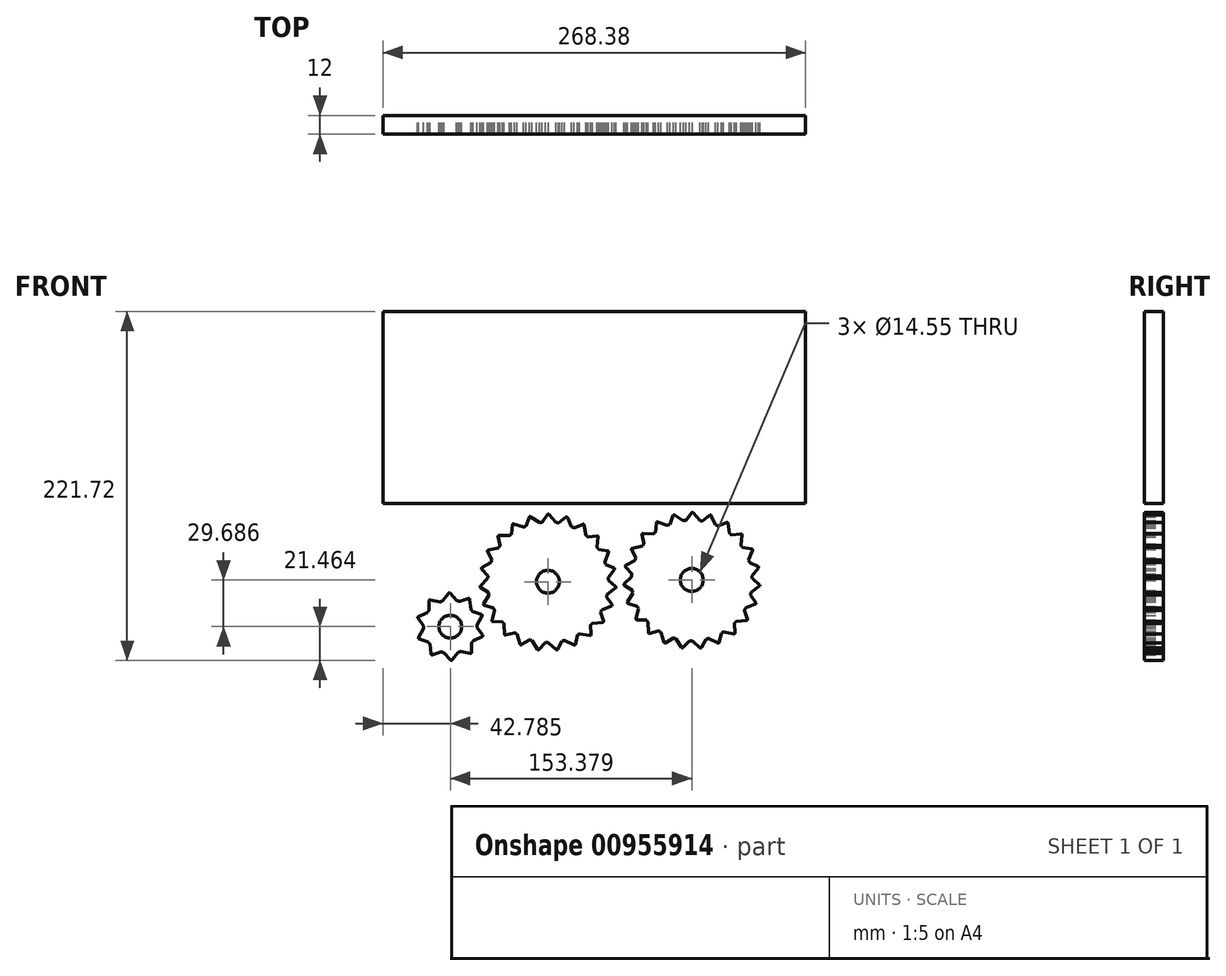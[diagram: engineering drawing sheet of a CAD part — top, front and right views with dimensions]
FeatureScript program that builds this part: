
annotation { "Feature Type Name" : "Feature", "Feature Type Description" : "" }
export const myFeature = defineFeature(function(context is Context, id is Id, definition is map)
    precondition{}
    {
        {
            var Q0;
            Q0=qCreatedBy(makeId("Front.planeOp"),FACE);
            var sketch = newSketch(context, id + "F0", { "sketchPlane" : qUnion([Q0])});
            skArc(sketch, "E0", {"start": v(-13.97, 35.72) * mm, "mid": v(-14.74, 35.41) * mm, "end": v(-15.5, 35.09) * mm});
            skCircle(sketch, "E1", {"center": v(-0.05, 0.37) * mm, "radius": 7.28 * mm});
            skLineSegment(sketch, "E2", {"start": v(-0.25, 43.01) * mm, "end": v(-3.81, 38.17) * mm});
            skLineSegment(sketch, "E3", {"start": v(4.99, 38.03) * mm, "end": v(0.67, 43.05) * mm});
            skArc(sketch, "E4.filletArc", {"start": v(0.67, 43.05) * mm, "mid": v(0.2, 43.25) * mm, "end": v(-0.25, 43.01) * mm});
            skLineSegment(sketch, "E5.1.0", {"start": v(-5.46, 37.97) * mm, "end": v(-10.97, 41.63) * mm});
            skLineSegment(sketch, "E5.1.1", {"start": v(-11.84, 41.35) * mm, "end": v(-13.97, 35.72) * mm});
            skArc(sketch, "E5.1.2", {"start": v(-10.97, 41.63) * mm, "mid": v(-11.47, 41.7) * mm, "end": v(-11.84, 41.35) * mm});
            skLineSegment(sketch, "E5.2.0", {"start": v(-15.5, 35.09) * mm, "end": v(-21.8, 37.13) * mm});
            skLineSegment(sketch, "E5.2.1", {"start": v(-22.56, 36.62) * mm, "end": v(-23.09, 30.63) * mm});
            skArc(sketch, "E5.2.2", {"start": v(-21.8, 37.13) * mm, "mid": v(-22.3, 37.06) * mm, "end": v(-22.56, 36.62) * mm});
            skLineSegment(sketch, "E5.3.0", {"start": v(-24.4, 29.6) * mm, "end": v(-31, 29.87) * mm});
            skLineSegment(sketch, "E5.3.1", {"start": v(-31.6, 29.18) * mm, "end": v(-30.5, 23.27) * mm});
            skArc(sketch, "E5.3.2", {"start": v(-31, 29.87) * mm, "mid": v(-31.47, 29.67) * mm, "end": v(-31.6, 29.18) * mm});
            skLineSegment(sketch, "E5.4.0", {"start": v(-31.47, 21.92) * mm, "end": v(-37.91, 20.4) * mm});
            skLineSegment(sketch, "E5.4.1", {"start": v(-38.3, 19.57) * mm, "end": v(-35.64, 14.18) * mm});
            skArc(sketch, "E5.4.2", {"start": v(-37.91, 20.4) * mm, "mid": v(-38.3, 20.08) * mm, "end": v(-38.3, 19.57) * mm});
            skLineSegment(sketch, "E5.5.0", {"start": v(-36.22, 12.62) * mm, "end": v(-42.01, 9.42) * mm});
            skLineSegment(sketch, "E5.5.1", {"start": v(-42.16, 8.5) * mm, "end": v(-38.14, 4.03) * mm});
            skArc(sketch, "E5.5.2", {"start": v(-42.01, 9.42) * mm, "mid": v(-42.3, 9) * mm, "end": v(-42.16, 8.5) * mm});
            skLineSegment(sketch, "E5.6.0", {"start": v(-38.28, 2.38) * mm, "end": v(-43, -2.27) * mm});
            skLineSegment(sketch, "E5.6.1", {"start": v(-42.9, -3.18) * mm, "end": v(-37.82, -6.4) * mm});
            skArc(sketch, "E5.6.2", {"start": v(-43, -2.27) * mm, "mid": v(-43.16, -2.75) * mm, "end": v(-42.9, -3.18) * mm});
            skLineSegment(sketch, "E5.7.0", {"start": v(-37.5, -8.04) * mm, "end": v(-40.79, -13.78) * mm});
            skLineSegment(sketch, "E5.7.1", {"start": v(-40.45, -14.64) * mm, "end": v(-34.69, -16.37) * mm});
            skArc(sketch, "E5.7.2", {"start": v(-40.79, -13.78) * mm, "mid": v(-40.82, -14.3) * mm, "end": v(-40.45, -14.64) * mm});
            skLineSegment(sketch, "E5.8.0", {"start": v(-33.95, -17.86) * mm, "end": v(-35.56, -24.28) * mm});
            skLineSegment(sketch, "E5.8.1", {"start": v(-35, -25) * mm, "end": v(-28.98, -25.12) * mm});
            skArc(sketch, "E5.8.2", {"start": v(-35.56, -24.28) * mm, "mid": v(-35.45, -24.78) * mm, "end": v(-35, -25) * mm});
            skLineSegment(sketch, "E5.9.0", {"start": v(-27.87, -26.36) * mm, "end": v(-27.69, -32.97) * mm});
            skLineSegment(sketch, "E5.9.1", {"start": v(-26.95, -33.52) * mm, "end": v(-21.13, -32.01) * mm});
            skArc(sketch, "E5.9.2", {"start": v(-27.69, -32.97) * mm, "mid": v(-27.45, -33.42) * mm, "end": v(-26.95, -33.52) * mm});
            skLineSegment(sketch, "E5.10.0", {"start": v(-19.73, -32.9) * mm, "end": v(-17.77, -39.22) * mm});
            skLineSegment(sketch, "E5.10.1", {"start": v(-16.9, -39.55) * mm, "end": v(-11.71, -36.53) * mm});
            skArc(sketch, "E5.10.2", {"start": v(-17.77, -39.22) * mm, "mid": v(-17.42, -39.6) * mm, "end": v(-16.9, -39.55) * mm});
            skLineSegment(sketch, "E5.11.0", {"start": v(-10.12, -37) * mm, "end": v(-6.53, -42.55) * mm});
            skLineSegment(sketch, "E5.11.1", {"start": v(-5.61, -42.65) * mm, "end": v(-1.42, -38.33) * mm});
            skArc(sketch, "E5.11.2", {"start": v(-6.53, -42.55) * mm, "mid": v(-6.1, -42.82) * mm, "end": v(-5.61, -42.65) * mm});
            skLineSegment(sketch, "E5.12.0", {"start": v(0.24, -38.36) * mm, "end": v(5.2, -42.74) * mm});
            skLineSegment(sketch, "E5.12.1", {"start": v(6.1, -42.58) * mm, "end": v(8.97, -37.3) * mm});
            skArc(sketch, "E5.12.2", {"start": v(5.2, -42.74) * mm, "mid": v(5.69, -42.88) * mm, "end": v(6.1, -42.58) * mm});
            skLineSegment(sketch, "E5.13.0", {"start": v(10.58, -36.87) * mm, "end": v(16.53, -39.75) * mm});
            skLineSegment(sketch, "E5.13.1", {"start": v(17.36, -39.35) * mm, "end": v(18.7, -33.49) * mm});
            skArc(sketch, "E5.13.2", {"start": v(16.53, -39.75) * mm, "mid": v(17.05, -39.75) * mm, "end": v(17.36, -39.35) * mm});
            skLineSegment(sketch, "E5.14.0", {"start": v(20.13, -32.65) * mm, "end": v(26.65, -33.82) * mm});
            skLineSegment(sketch, "E5.14.1", {"start": v(27.34, -33.2) * mm, "end": v(27.04, -27.2) * mm});
            skArc(sketch, "E5.14.2", {"start": v(26.65, -33.82) * mm, "mid": v(27.14, -33.68) * mm, "end": v(27.34, -33.2) * mm});
            skLineSegment(sketch, "E5.15.0", {"start": v(28.2, -26) * mm, "end": v(34.78, -25.37) * mm});
            skLineSegment(sketch, "E5.15.1", {"start": v(35.28, -24.6) * mm, "end": v(33.38, -18.9) * mm});
            skArc(sketch, "E5.15.2", {"start": v(34.78, -25.37) * mm, "mid": v(35.22, -25.1) * mm, "end": v(35.28, -24.6) * mm});
            skLineSegment(sketch, "E5.16.0", {"start": v(34.17, -17.43) * mm, "end": v(40.34, -15.05) * mm});
            skLineSegment(sketch, "E5.16.1", {"start": v(40.61, -14.17) * mm, "end": v(37.24, -9.2) * mm});
            skArc(sketch, "E5.16.2", {"start": v(40.34, -15.05) * mm, "mid": v(40.69, -14.68) * mm, "end": v(40.61, -14.17) * mm});
            skLineSegment(sketch, "E5.17.0", {"start": v(37.6, -7.57) * mm, "end": v(42.9, -3.6) * mm});
            skLineSegment(sketch, "E5.17.1", {"start": v(42.93, -2.69) * mm, "end": v(38.34, 1.2) * mm});
            skArc(sketch, "E5.17.2", {"start": v(42.9, -3.6) * mm, "mid": v(43.14, -3.15) * mm, "end": v(42.93, -2.69) * mm});
            skLineSegment(sketch, "E5.18.0", {"start": v(38.25, 2.86) * mm, "end": v(42.28, 8.1) * mm});
            skLineSegment(sketch, "E5.18.1", {"start": v(42.06, 9) * mm, "end": v(36.6, 11.5) * mm});
            skArc(sketch, "E5.18.2", {"start": v(42.28, 8.1) * mm, "mid": v(42.39, 8.6) * mm, "end": v(42.06, 9) * mm});
            skLineSegment(sketch, "E5.19.0", {"start": v(36.06, 13.07) * mm, "end": v(38.53, 19.2) * mm});
            skLineSegment(sketch, "E5.19.1", {"start": v(38.08, 20) * mm, "end": v(32.14, 20.94) * mm});
            skArc(sketch, "E5.19.2", {"start": v(38.53, 19.2) * mm, "mid": v(38.5, 19.72) * mm, "end": v(38.08, 20) * mm});
            skLineSegment(sketch, "E5.20.0", {"start": v(31.2, 22.31) * mm, "end": v(31.92, 28.9) * mm});
            skLineSegment(sketch, "E5.20.1", {"start": v(31.27, 29.54) * mm, "end": v(25.3, 28.84) * mm});
            skArc(sketch, "E5.20.2", {"start": v(31.92, 28.9) * mm, "mid": v(31.75, 29.37) * mm, "end": v(31.27, 29.54) * mm});
            skLineSegment(sketch, "E5.21.0", {"start": v(24.02, 29.9) * mm, "end": v(22.94, 36.43) * mm});
            skLineSegment(sketch, "E5.21.1", {"start": v(22.14, 36.88) * mm, "end": v(16.58, 34.6) * mm});
            skArc(sketch, "E5.21.2", {"start": v(22.94, 36.43) * mm, "mid": v(22.65, 36.85) * mm, "end": v(22.14, 36.88) * mm});
            skLineSegment(sketch, "E5.22.0", {"start": v(15.06, 35.28) * mm, "end": v(12.26, 41.27) * mm});
            skLineSegment(sketch, "E5.22.1", {"start": v(11.36, 41.48) * mm, "end": v(6.63, 37.78) * mm});
            skArc(sketch, "E5.22.2", {"start": v(12.26, 41.27) * mm, "mid": v(11.86, 41.6) * mm, "end": v(11.36, 41.48) * mm});
            skArc(sketch, "E6.trimOffspring", {"start": v(-23.09, 30.63) * mm, "mid": v(-23.75, 30.12) * mm, "end": v(-24.4, 29.6) * mm});
            skArc(sketch, "E7.trimOffspring", {"start": v(-30.5, 23.27) * mm, "mid": v(-31, 22.6) * mm, "end": v(-31.47, 21.92) * mm});
            skArc(sketch, "E8.trimOffspring", {"start": v(-35.64, 14.18) * mm, "mid": v(-35.94, 13.4) * mm, "end": v(-36.22, 12.62) * mm});
            skArc(sketch, "E9.trimOffspring", {"start": v(-38.14, 4.03) * mm, "mid": v(-38.22, 3.2) * mm, "end": v(-38.28, 2.38) * mm});
            skArc(sketch, "E10.trimOffspring", {"start": v(-37.82, -6.4) * mm, "mid": v(-37.67, -7.22) * mm, "end": v(-37.5, -8.04) * mm});
            skArc(sketch, "E11.trimOffspring", {"start": v(-34.69, -16.37) * mm, "mid": v(-34.33, -17.12) * mm, "end": v(-33.95, -17.86) * mm});
            skArc(sketch, "E12.trimOffspring", {"start": v(-28.98, -25.12) * mm, "mid": v(-28.43, -25.75) * mm, "end": v(-27.87, -26.36) * mm});
            skArc(sketch, "E13.trimOffspring", {"start": v(-21.13, -32.01) * mm, "mid": v(-20.43, -32.46) * mm, "end": v(-19.73, -32.9) * mm});
            skArc(sketch, "E14.trimOffspring", {"start": v(-11.71, -36.53) * mm, "mid": v(-10.92, -36.77) * mm, "end": v(-10.12, -37) * mm});
            skArc(sketch, "E15.trimOffspring", {"start": v(-1.42, -38.33) * mm, "mid": v(-0.6, -38.35) * mm, "end": v(0.24, -38.36) * mm});
            skArc(sketch, "E16.trimOffspring", {"start": v(8.97, -37.3) * mm, "mid": v(9.78, -37.1) * mm, "end": v(10.58, -36.87) * mm});
            skArc(sketch, "E17.trimOffspring", {"start": v(18.7, -33.49) * mm, "mid": v(19.42, -33.08) * mm, "end": v(20.13, -32.65) * mm});
            skArc(sketch, "E18.trimOffspring", {"start": v(27.04, -27.2) * mm, "mid": v(27.63, -26.61) * mm, "end": v(28.2, -26) * mm});
            skArc(sketch, "E19.trimOffspring", {"start": v(33.38, -18.9) * mm, "mid": v(33.78, -18.17) * mm, "end": v(34.17, -17.43) * mm});
            skArc(sketch, "E20.trimOffspring", {"start": v(37.24, -9.2) * mm, "mid": v(37.43, -8.38) * mm, "end": v(37.6, -7.57) * mm});
            skArc(sketch, "E21.trimOffspring", {"start": v(38.34, 1.2) * mm, "mid": v(38.3, 2.03) * mm, "end": v(38.25, 2.86) * mm});
            skArc(sketch, "E22.trimOffspring", {"start": v(36.6, 11.5) * mm, "mid": v(36.34, 12.29) * mm, "end": v(36.06, 13.07) * mm});
            skArc(sketch, "E23.trimOffspring", {"start": v(32.14, 20.94) * mm, "mid": v(31.67, 21.63) * mm, "end": v(31.2, 22.31) * mm});
            skArc(sketch, "E24.trimOffspring", {"start": v(25.3, 28.84) * mm, "mid": v(24.66, 29.38) * mm, "end": v(24.02, 29.9) * mm});
            skArc(sketch, "E25.trimOffspring", {"start": v(16.58, 34.6) * mm, "mid": v(15.82, 34.94) * mm, "end": v(15.06, 35.28) * mm});
            skArc(sketch, "E26.trimOffspring", {"start": v(6.63, 37.78) * mm, "mid": v(5.8, 37.92) * mm, "end": v(4.99, 38.03) * mm});
            skArc(sketch, "E27.trimOffspring", {"start": v(-3.81, 38.17) * mm, "mid": v(-4.64, 38.08) * mm, "end": v(-5.46, 37.97) * mm});
            skArc(sketch, "E28", {"start": v(77.43, 36.88) * mm, "mid": v(76.66, 36.57) * mm, "end": v(75.9, 36.24) * mm});
            skCircle(sketch, "E29", {"center": v(91.34, 1.52) * mm, "radius": 7.28 * mm});
            skLineSegment(sketch, "E30", {"start": v(91.15, 44.17) * mm, "end": v(87.58, 39.32) * mm});
            skLineSegment(sketch, "E31", {"start": v(96.38, 39.19) * mm, "end": v(92.07, 44.2) * mm});
            skArc(sketch, "E32.filletArc", {"start": v(92.07, 44.2) * mm, "mid": v(91.6, 44.4) * mm, "end": v(91.15, 44.17) * mm});
            skLineSegment(sketch, "E33.1.0", {"start": v(85.94, 39.12) * mm, "end": v(80.43, 42.79) * mm});
            skLineSegment(sketch, "E33.1.1", {"start": v(79.55, 42.5) * mm, "end": v(77.43, 36.88) * mm});
            skArc(sketch, "E33.1.2", {"start": v(80.43, 42.79) * mm, "mid": v(79.92, 42.86) * mm, "end": v(79.55, 42.5) * mm});
            skLineSegment(sketch, "E33.2.0", {"start": v(75.9, 36.24) * mm, "end": v(69.6, 38.28) * mm});
            skLineSegment(sketch, "E33.2.1", {"start": v(68.83, 37.78) * mm, "end": v(68.3, 31.79) * mm});
            skArc(sketch, "E33.2.2", {"start": v(69.6, 38.28) * mm, "mid": v(69.1, 38.21) * mm, "end": v(68.83, 37.78) * mm});
            skLineSegment(sketch, "E33.3.0", {"start": v(67, 30.76) * mm, "end": v(60.4, 31.03) * mm});
            skLineSegment(sketch, "E33.3.1", {"start": v(59.8, 30.33) * mm, "end": v(60.9, 24.42) * mm});
            skArc(sketch, "E33.3.2", {"start": v(60.4, 31.03) * mm, "mid": v(59.92, 30.82) * mm, "end": v(59.8, 30.33) * mm});
            skLineSegment(sketch, "E33.4.0", {"start": v(59.92, 23.08) * mm, "end": v(53.48, 21.56) * mm});
            skLineSegment(sketch, "E33.4.1", {"start": v(53.1, 20.72) * mm, "end": v(55.75, 15.33) * mm});
            skArc(sketch, "E33.4.2", {"start": v(53.48, 21.56) * mm, "mid": v(53.09, 21.23) * mm, "end": v(53.1, 20.72) * mm});
            skLineSegment(sketch, "E33.5.0", {"start": v(55.17, 13.77) * mm, "end": v(49.39, 10.57) * mm});
            skLineSegment(sketch, "E33.5.1", {"start": v(49.23, 9.66) * mm, "end": v(53.25, 5.19) * mm});
            skArc(sketch, "E33.5.2", {"start": v(49.39, 10.57) * mm, "mid": v(49.09, 10.15) * mm, "end": v(49.23, 9.66) * mm});
            skLineSegment(sketch, "E33.6.0", {"start": v(53.11, 3.53) * mm, "end": v(48.4, -1.11) * mm});
            skLineSegment(sketch, "E33.6.1", {"start": v(48.5, -2.03) * mm, "end": v(53.58, -5.25) * mm});
            skArc(sketch, "E33.6.2", {"start": v(48.4, -1.11) * mm, "mid": v(48.23, -1.6) * mm, "end": v(48.5, -2.03) * mm});
            skLineSegment(sketch, "E33.7.0", {"start": v(53.89, -6.88) * mm, "end": v(50.6, -12.63) * mm});
            skLineSegment(sketch, "E33.7.1", {"start": v(50.95, -13.48) * mm, "end": v(56.7, -15.22) * mm});
            skArc(sketch, "E33.7.2", {"start": v(50.6, -12.63) * mm, "mid": v(50.57, -13.14) * mm, "end": v(50.95, -13.48) * mm});
            skLineSegment(sketch, "E33.8.0", {"start": v(57.45, -16.7) * mm, "end": v(55.84, -23.12) * mm});
            skLineSegment(sketch, "E33.8.1", {"start": v(56.4, -23.85) * mm, "end": v(62.41, -23.97) * mm});
            skArc(sketch, "E33.8.2", {"start": v(55.84, -23.12) * mm, "mid": v(55.94, -23.62) * mm, "end": v(56.4, -23.85) * mm});
            skLineSegment(sketch, "E33.9.0", {"start": v(63.53, -25.2) * mm, "end": v(63.7, -31.81) * mm});
            skLineSegment(sketch, "E33.9.1", {"start": v(64.44, -32.37) * mm, "end": v(70.26, -30.86) * mm});
            skArc(sketch, "E33.9.2", {"start": v(63.7, -31.81) * mm, "mid": v(63.94, -32.27) * mm, "end": v(64.44, -32.37) * mm});
            skLineSegment(sketch, "E33.10.0", {"start": v(71.67, -31.74) * mm, "end": v(73.63, -38.06) * mm});
            skLineSegment(sketch, "E33.10.1", {"start": v(74.49, -38.4) * mm, "end": v(79.69, -35.37) * mm});
            skArc(sketch, "E33.10.2", {"start": v(73.63, -38.06) * mm, "mid": v(73.98, -38.44) * mm, "end": v(74.49, -38.4) * mm});
            skLineSegment(sketch, "E33.11.0", {"start": v(81.28, -35.85) * mm, "end": v(84.87, -41.4) * mm});
            skLineSegment(sketch, "E33.11.1", {"start": v(85.79, -41.5) * mm, "end": v(89.97, -37.18) * mm});
            skArc(sketch, "E33.11.2", {"start": v(84.87, -41.4) * mm, "mid": v(85.3, -41.67) * mm, "end": v(85.79, -41.5) * mm});
            skLineSegment(sketch, "E33.12.0", {"start": v(91.63, -37.2) * mm, "end": v(96.6, -41.58) * mm});
            skLineSegment(sketch, "E33.12.1", {"start": v(97.5, -41.42) * mm, "end": v(100.37, -36.14) * mm});
            skArc(sketch, "E33.12.2", {"start": v(96.6, -41.58) * mm, "mid": v(97.08, -41.72) * mm, "end": v(97.5, -41.42) * mm});
            skLineSegment(sketch, "E33.13.0", {"start": v(101.97, -35.72) * mm, "end": v(107.93, -38.6) * mm});
            skLineSegment(sketch, "E33.13.1", {"start": v(108.76, -38.2) * mm, "end": v(110.1, -32.34) * mm});
            skArc(sketch, "E33.13.2", {"start": v(107.93, -38.6) * mm, "mid": v(108.44, -38.6) * mm, "end": v(108.76, -38.2) * mm});
            skLineSegment(sketch, "E33.14.0", {"start": v(111.53, -31.5) * mm, "end": v(118.04, -32.66) * mm});
            skLineSegment(sketch, "E33.14.1", {"start": v(118.73, -32.05) * mm, "end": v(118.44, -26.05) * mm});
            skArc(sketch, "E33.14.2", {"start": v(118.04, -32.66) * mm, "mid": v(118.53, -32.53) * mm, "end": v(118.73, -32.05) * mm});
            skLineSegment(sketch, "E33.15.0", {"start": v(119.6, -24.85) * mm, "end": v(126.18, -24.22) * mm});
            skLineSegment(sketch, "E33.15.1", {"start": v(126.68, -23.45) * mm, "end": v(124.78, -17.74) * mm});
            skArc(sketch, "E33.15.2", {"start": v(126.18, -24.22) * mm, "mid": v(126.61, -23.95) * mm, "end": v(126.68, -23.45) * mm});
            skLineSegment(sketch, "E33.16.0", {"start": v(125.56, -16.28) * mm, "end": v(131.73, -13.9) * mm});
            skLineSegment(sketch, "E33.16.1", {"start": v(132, -13.02) * mm, "end": v(128.64, -8.04) * mm});
            skArc(sketch, "E33.16.2", {"start": v(131.73, -13.9) * mm, "mid": v(132.08, -13.52) * mm, "end": v(132, -13.02) * mm});
            skLineSegment(sketch, "E33.17.0", {"start": v(129, -6.42) * mm, "end": v(134.3, -2.45) * mm});
            skLineSegment(sketch, "E33.17.1", {"start": v(134.32, -1.53) * mm, "end": v(129.73, 2.35) * mm});
            skArc(sketch, "E33.17.2", {"start": v(134.3, -2.45) * mm, "mid": v(134.53, -2) * mm, "end": v(134.32, -1.53) * mm});
            skLineSegment(sketch, "E33.18.0", {"start": v(129.65, 4) * mm, "end": v(133.68, 9.25) * mm});
            skLineSegment(sketch, "E33.18.1", {"start": v(133.46, 10.15) * mm, "end": v(127.99, 12.65) * mm});
            skArc(sketch, "E33.18.2", {"start": v(133.68, 9.25) * mm, "mid": v(133.78, 9.76) * mm, "end": v(133.46, 10.15) * mm});
            skLineSegment(sketch, "E33.19.0", {"start": v(127.46, 14.22) * mm, "end": v(129.93, 20.36) * mm});
            skLineSegment(sketch, "E33.19.1", {"start": v(129.47, 21.16) * mm, "end": v(123.53, 22.1) * mm});
            skArc(sketch, "E33.19.2", {"start": v(129.93, 20.36) * mm, "mid": v(129.9, 20.87) * mm, "end": v(129.47, 21.16) * mm});
            skLineSegment(sketch, "E33.20.0", {"start": v(122.6, 23.47) * mm, "end": v(123.32, 30.05) * mm});
            skLineSegment(sketch, "E33.20.1", {"start": v(122.66, 30.7) * mm, "end": v(116.69, 30) * mm});
            skArc(sketch, "E33.20.2", {"start": v(123.32, 30.05) * mm, "mid": v(123.14, 30.53) * mm, "end": v(122.66, 30.7) * mm});
            skLineSegment(sketch, "E33.21.0", {"start": v(115.42, 31.06) * mm, "end": v(114.34, 37.59) * mm});
            skLineSegment(sketch, "E33.21.1", {"start": v(113.53, 38.03) * mm, "end": v(107.97, 35.75) * mm});
            skArc(sketch, "E33.21.2", {"start": v(114.34, 37.59) * mm, "mid": v(114.04, 38) * mm, "end": v(113.53, 38.03) * mm});
            skLineSegment(sketch, "E33.22.0", {"start": v(106.46, 36.43) * mm, "end": v(103.66, 42.42) * mm});
            skLineSegment(sketch, "E33.22.1", {"start": v(102.76, 42.64) * mm, "end": v(98.02, 38.93) * mm});
            skArc(sketch, "E33.22.2", {"start": v(103.66, 42.42) * mm, "mid": v(103.26, 42.75) * mm, "end": v(102.76, 42.64) * mm});
            skArc(sketch, "E34.trimOffspring", {"start": v(68.3, 31.79) * mm, "mid": v(67.65, 31.28) * mm, "end": v(67, 30.76) * mm});
            skArc(sketch, "E35.trimOffspring", {"start": v(60.9, 24.42) * mm, "mid": v(60.4, 23.75) * mm, "end": v(59.92, 23.08) * mm});
            skArc(sketch, "E36.trimOffspring", {"start": v(55.75, 15.33) * mm, "mid": v(55.46, 14.56) * mm, "end": v(55.17, 13.77) * mm});
            skArc(sketch, "E37.trimOffspring", {"start": v(53.25, 5.19) * mm, "mid": v(53.17, 4.36) * mm, "end": v(53.11, 3.53) * mm});
            skArc(sketch, "E38.trimOffspring", {"start": v(53.58, -5.25) * mm, "mid": v(53.72, -6.07) * mm, "end": v(53.89, -6.88) * mm});
            skArc(sketch, "E39.trimOffspring", {"start": v(56.7, -15.22) * mm, "mid": v(57.07, -15.97) * mm, "end": v(57.45, -16.7) * mm});
            skArc(sketch, "E40.trimOffspring", {"start": v(62.41, -23.97) * mm, "mid": v(62.96, -24.6) * mm, "end": v(63.53, -25.2) * mm});
            skArc(sketch, "E41.trimOffspring", {"start": v(70.26, -30.86) * mm, "mid": v(70.96, -31.3) * mm, "end": v(71.67, -31.74) * mm});
            skArc(sketch, "E42.trimOffspring", {"start": v(79.69, -35.37) * mm, "mid": v(80.48, -35.62) * mm, "end": v(81.28, -35.85) * mm});
            skArc(sketch, "E43.trimOffspring", {"start": v(89.97, -37.18) * mm, "mid": v(90.8, -37.2) * mm, "end": v(91.63, -37.2) * mm});
            skArc(sketch, "E44.trimOffspring", {"start": v(100.37, -36.14) * mm, "mid": v(101.17, -35.94) * mm, "end": v(101.97, -35.72) * mm});
            skArc(sketch, "E45.trimOffspring", {"start": v(110.1, -32.34) * mm, "mid": v(110.82, -31.92) * mm, "end": v(111.53, -31.5) * mm});
            skArc(sketch, "E46.trimOffspring", {"start": v(118.44, -26.05) * mm, "mid": v(119.02, -25.46) * mm, "end": v(119.6, -24.85) * mm});
            skArc(sketch, "E47.trimOffspring", {"start": v(124.78, -17.74) * mm, "mid": v(125.18, -17.02) * mm, "end": v(125.56, -16.28) * mm});
            skArc(sketch, "E48.trimOffspring", {"start": v(128.64, -8.04) * mm, "mid": v(128.83, -7.23) * mm, "end": v(129, -6.42) * mm});
            skArc(sketch, "E49.trimOffspring", {"start": v(129.73, 2.35) * mm, "mid": v(129.7, 3.18) * mm, "end": v(129.65, 4) * mm});
            skArc(sketch, "E50.trimOffspring", {"start": v(127.99, 12.65) * mm, "mid": v(127.73, 13.44) * mm, "end": v(127.46, 14.22) * mm});
            skArc(sketch, "E51.trimOffspring", {"start": v(123.53, 22.1) * mm, "mid": v(123.07, 22.79) * mm, "end": v(122.6, 23.47) * mm});
            skArc(sketch, "E52.trimOffspring", {"start": v(116.69, 30) * mm, "mid": v(116.06, 30.53) * mm, "end": v(115.42, 31.06) * mm});
            skArc(sketch, "E53.trimOffspring", {"start": v(107.97, 35.75) * mm, "mid": v(107.22, 36.1) * mm, "end": v(106.46, 36.43) * mm});
            skArc(sketch, "E54.trimOffspring", {"start": v(98.02, 38.93) * mm, "mid": v(97.2, 39.07) * mm, "end": v(96.38, 39.19) * mm});
            skArc(sketch, "E55.trimOffspring", {"start": v(87.58, 39.32) * mm, "mid": v(86.76, 39.23) * mm, "end": v(85.94, 39.12) * mm});
            skLineSegment(sketch, "E56", {"start": v(-63.24, -6.94) * mm, "end": v(-66.8, -11.79) * mm});
            skLineSegment(sketch, "E57", {"start": v(-57.96, -11.6) * mm, "end": v(-62.33, -6.89) * mm});
            skArc(sketch, "E58", {"start": v(-66.8, -11.79) * mm, "mid": v(-67.65, -12.06) * mm, "end": v(-68.48, -12.37) * mm});
            skLineSegment(sketch, "E59.1.0", {"start": v(-75.48, -11.7) * mm, "end": v(-75.52, -17.72) * mm});
            skLineSegment(sketch, "E59.1.1", {"start": v(-68.48, -12.37) * mm, "end": v(-74.78, -11.13) * mm});
            skLineSegment(sketch, "E59.2.0", {"start": v(-82.6, -22.75) * mm, "end": v(-79.09, -27.64) * mm});
            skLineSegment(sketch, "E59.2.1", {"start": v(-76.53, -19.17) * mm, "end": v(-82.36, -21.87) * mm});
            skLineSegment(sketch, "E59.3.0", {"start": v(-81.85, -35.87) * mm, "end": v(-76.14, -37.76) * mm});
            skLineSegment(sketch, "E59.3.1", {"start": v(-79.05, -29.4) * mm, "end": v(-82.18, -35.02) * mm});
            skLineSegment(sketch, "E59.4.0", {"start": v(-73.54, -46.04) * mm, "end": v(-67.8, -44.22) * mm});
            skLineSegment(sketch, "E59.4.1", {"start": v(-75.07, -39.17) * mm, "end": v(-74.3, -45.55) * mm});
            skLineSegment(sketch, "E59.5.0", {"start": v(-60.83, -49.39) * mm, "end": v(-57.27, -44.55) * mm});
            skLineSegment(sketch, "E59.5.1", {"start": v(-66.1, -44.73) * mm, "end": v(-61.74, -49.44) * mm});
            skLineSegment(sketch, "E59.6.0", {"start": v(-48.59, -44.63) * mm, "end": v(-48.55, -38.62) * mm});
            skLineSegment(sketch, "E59.6.1", {"start": v(-55.6, -43.96) * mm, "end": v(-49.29, -45.2) * mm});
            skLineSegment(sketch, "E59.7.0", {"start": v(-41.48, -33.58) * mm, "end": v(-44.98, -28.7) * mm});
            skLineSegment(sketch, "E59.7.1", {"start": v(-47.54, -37.16) * mm, "end": v(-41.7, -34.46) * mm});
            skLineSegment(sketch, "E59.8.0", {"start": v(-42.22, -20.46) * mm, "end": v(-47.93, -18.57) * mm});
            skLineSegment(sketch, "E59.8.1", {"start": v(-45.02, -26.92) * mm, "end": v(-41.9, -21.3) * mm});
            skLineSegment(sketch, "E59.9.0", {"start": v(-50.53, -10.29) * mm, "end": v(-56.26, -12.11) * mm});
            skLineSegment(sketch, "E59.9.1", {"start": v(-49, -17.16) * mm, "end": v(-49.77, -10.78) * mm});
            skArc(sketch, "E60.filletArc", {"start": v(-62.33, -6.89) * mm, "mid": v(-62.8, -6.7) * mm, "end": v(-63.24, -6.94) * mm});
            skArc(sketch, "E61.1.0", {"start": v(-74.78, -11.13) * mm, "mid": v(-75.27, -11.25) * mm, "end": v(-75.48, -11.7) * mm});
            skArc(sketch, "E61.2.0", {"start": v(-82.36, -21.87) * mm, "mid": v(-82.68, -22.26) * mm, "end": v(-82.6, -22.75) * mm});
            skArc(sketch, "E61.3.0", {"start": v(-82.18, -35.02) * mm, "mid": v(-82.21, -35.52) * mm, "end": v(-81.85, -35.87) * mm});
            skArc(sketch, "E61.4.0", {"start": v(-74.3, -45.55) * mm, "mid": v(-74.03, -45.98) * mm, "end": v(-73.54, -46.04) * mm});
            skArc(sketch, "E61.5.0", {"start": v(-61.74, -49.44) * mm, "mid": v(-61.27, -49.63) * mm, "end": v(-60.83, -49.39) * mm});
            skArc(sketch, "E61.6.0", {"start": v(-49.29, -45.2) * mm, "mid": v(-48.8, -45.08) * mm, "end": v(-48.59, -44.63) * mm});
            skArc(sketch, "E61.7.0", {"start": v(-41.7, -34.46) * mm, "mid": v(-41.39, -34.07) * mm, "end": v(-41.48, -33.58) * mm});
            skArc(sketch, "E61.8.0", {"start": v(-41.9, -21.3) * mm, "mid": v(-41.86, -20.8) * mm, "end": v(-42.22, -20.46) * mm});
            skArc(sketch, "E61.9.0", {"start": v(-49.77, -10.78) * mm, "mid": v(-50.04, -10.35) * mm, "end": v(-50.53, -10.29) * mm});
            skCircle(sketch, "E62", {"center": v(-62.04, -28.17) * mm, "radius": 7.28 * mm});
            skArc(sketch, "E63.trimOffspring", {"start": v(-56.26, -12.11) * mm, "mid": v(-57.1, -11.83) * mm, "end": v(-57.96, -11.6) * mm});
            skArc(sketch, "E64.trimOffspring", {"start": v(-47.93, -18.57) * mm, "mid": v(-48.45, -17.85) * mm, "end": v(-49, -17.16) * mm});
            skArc(sketch, "E65.trimOffspring", {"start": v(-44.98, -28.7) * mm, "mid": v(-44.98, -27.8) * mm, "end": v(-45.02, -26.92) * mm});
            skArc(sketch, "E66.trimOffspring", {"start": v(-48.55, -38.62) * mm, "mid": v(-48.03, -37.9) * mm, "end": v(-47.54, -37.16) * mm});
            skArc(sketch, "E67.trimOffspring", {"start": v(-57.27, -44.55) * mm, "mid": v(-56.42, -44.28) * mm, "end": v(-55.6, -43.96) * mm});
            skArc(sketch, "E68.trimOffspring", {"start": v(-67.8, -44.22) * mm, "mid": v(-66.97, -44.5) * mm, "end": v(-66.1, -44.73) * mm});
            skArc(sketch, "E69.trimOffspring", {"start": v(-76.14, -37.76) * mm, "mid": v(-75.62, -38.48) * mm, "end": v(-75.07, -39.17) * mm});
            skArc(sketch, "E70.trimOffspring", {"start": v(-79.09, -27.64) * mm, "mid": v(-79.1, -28.52) * mm, "end": v(-79.05, -29.4) * mm});
            skArc(sketch, "E71.trimOffspring", {"start": v(-75.52, -17.72) * mm, "mid": v(-76.04, -18.43) * mm, "end": v(-76.53, -19.17) * mm});
            skLineSegment(sketch, "E72.bottom", {"start": v(-104.82, 172.1) * mm, "end": v(163.56, 172.1) * mm});
            skLineSegment(sketch, "E72.top", {"start": v(-104.82, 50.06) * mm, "end": v(163.56, 50.06) * mm});
            skLineSegment(sketch, "E72.left", {"start": v(-104.82, 172.1) * mm, "end": v(-104.82, 50.06) * mm});
            skLineSegment(sketch, "E72.right", {"start": v(163.56, 172.1) * mm, "end": v(163.56, 50.06) * mm});
            skSolve(sketch);
        }
        {
            var Q0;
            Q0 = qSketchRegion(id + "F0", true);
            extrude(context, id + "F1", {"entities" : qUnion([Q0]), "depth" : 12 * mm, "offsetDistance" : 25 * mm});
        }
        {
            var Q0;
            Q0 = qSketchRegion(id + "F0", true);
            extrude(context, id + "F2", {"entities" : qUnion([Q0]), "operationType" : NewBodyOperationType.ADD, "depth" : 12 * mm, "offsetDistance" : 25 * mm});
        }
    });
